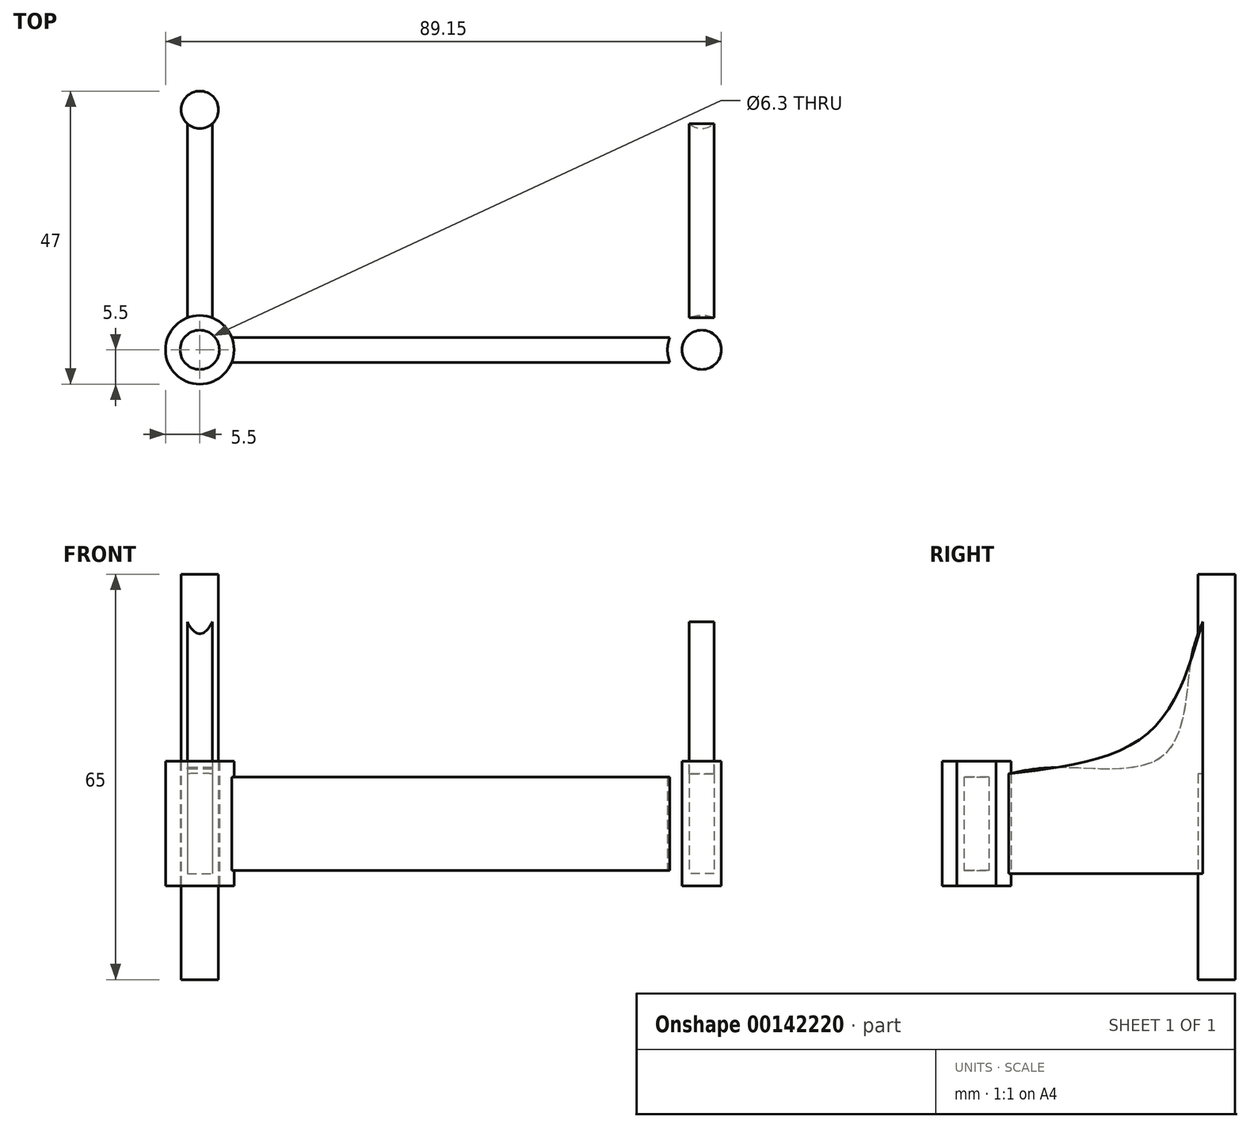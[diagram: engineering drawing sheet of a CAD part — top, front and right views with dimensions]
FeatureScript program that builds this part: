
annotation { "Feature Type Name" : "Feature", "Feature Type Description" : "" }
export const myFeature = defineFeature(function(context is Context, id is Id, definition is map)
    precondition{}
    {
        {
            var Q0;
            Q0=qCreatedBy(makeId("Top.planeOp"),FACE);
            var sketch = newSketch(context, id + "F0", { "sketchPlane" : qUnion([Q0])});
            skLineSegment(sketch, "E0.0", {"start": v(-35.13, -52) * mm, "end": v(0, -52) * mm});
            skLineSegment(sketch, "E1.0", {"start": v(-35.13, -48) * mm, "end": v(0, -48) * mm});
            skCircle(sketch, "E2", {"center": v(-40.25, -11.5) * mm, "radius": 3 * mm});
            skCircle(sketch, "E3", {"center": v(-40.25, -50) * mm, "radius": 3.15 * mm});
            skPoint(sketch, "E4", {"position": v(-42.25, -44.88) * mm});
            skPoint(sketch, "E5", {"position": v(-38.25, -44.88) * mm});
            skPoint(sketch, "E6", {"position": v(-42.25, -13.74) * mm});
            skPoint(sketch, "E7", {"position": v(-38.25, -13.74) * mm});
            skLineSegment(sketch, "E8", {"start": v(-42.25, -44.88) * mm, "end": v(-42.25, -13.74) * mm});
            skLineSegment(sketch, "E9", {"start": v(-38.25, -13.74) * mm, "end": v(-38.25, -44.88) * mm});
            skCircle(sketch, "E10", {"center": v(-40.25, -50) * mm, "radius": 5.5 * mm});
            skPoint(sketch, "E11.MirrorP", {"position": v(38.25, -44.88) * mm});
            skPoint(sketch, "E12.MirrorP", {"position": v(42.25, -44.88) * mm});
            skLineSegment(sketch, "E13.MirrorCS", {"start": v(35.13, -48) * mm, "end": v(0, -48) * mm});
            skLineSegment(sketch, "E14.MirrorCS", {"start": v(42.25, -44.88) * mm, "end": v(42.25, -13.74) * mm});
            skPoint(sketch, "E15.MirrorP", {"position": v(42.25, -13.74) * mm});
            skCircle(sketch, "E16.MirrorC", {"center": v(40.25, -50) * mm, "radius": 5.5 * mm});
            skPoint(sketch, "E17.MirrorP", {"position": v(38.25, -13.74) * mm});
            skCircle(sketch, "E18.MirrorC", {"center": v(40.25, -11.5) * mm, "radius": 3 * mm});
            skLineSegment(sketch, "E19.MirrorCS", {"start": v(38.25, -13.74) * mm, "end": v(38.25, -44.88) * mm});
            skLineSegment(sketch, "E20.MirrorCS", {"start": v(35.13, -52) * mm, "end": v(0, -52) * mm});
            skCircle(sketch, "E21.MirrorC", {"center": v(40.25, -50) * mm, "radius": 3.15 * mm});
            skSolve(sketch);
        }
        {
            var Q0;
            Q0=makeQuery(id+"F0.imprint","IMPRINT",FACE,{"disambiguationData":[TD([[makeQuery(id+"F0.imprint","IMPRINT",EDGE,{"derivedFrom":sQuery(id+"F0.wireOp",EDGE,"E3")}),-1.0]])]});
            var Q1;
            Q1=makeQuery(id+"F0.imprint","IMPRINT",FACE,{"disambiguationData":[TD([[makeQuery(id+"F0.imprint","IMPRINT",EDGE,{"derivedFrom":sQuery(id+"F0.wireOp",EDGE,"E21.MirrorC")}),1.0]])]});
            extrude(context, id + "F1", {"entities" : qUnion([Q0, Q1]), "depth" : 20 * mm, "symmetric" : true});
        }
        {
            var Q0;
            {var subQ2=sQuery(id+"F0.wireOp",EDGE,"E0.0");Q0=makeQuery(id+"F0.imprint","IMPRINT",FACE,{"disambiguationData":[TD([[makeQuery(id+"F0.imprint","IMPRINT",EDGE,{"derivedFrom":subQ2}),1.0]])]});}
            extrude(context, id + "F2", {"entities" : qUnion([Q0]), "operationType" : NewBodyOperationType.ADD, "depth" : 15 * mm, "symmetric" : true});
        }
        {
            var Q0;
            {var subQ0=sQuery(id+"F0.wireOp",EDGE,"E14.MirrorCS");Q0=makeQuery(id+"F0.imprint","IMPRINT",FACE,{"disambiguationData":[TD([[makeQuery(id+"F0.imprint","IMPRINT",EDGE,{"derivedFrom":subQ0}),1.0]])]});}
            var Q1;
            {var subQ0=sQuery(id+"F0.wireOp",EDGE,"E8");Q1=makeQuery(id+"F0.imprint","IMPRINT",FACE,{"disambiguationData":[TD([[makeQuery(id+"F0.imprint","IMPRINT",EDGE,{"derivedFrom":subQ0}),-1.0]])]});}
            extrude(context, id + "F3", {"entities" : qUnion([Q0, Q1]), "operationType" : NewBodyOperationType.ADD, "depth" : 16 * mm, "symmetric" : true});
        }
        {
            var Q0;
            {var subQ0=sQuery(id+"F0.wireOp",EDGE,"E2");var subQ1=makeQuery(id+"F0.imprint","INTERSECT",VERTEX,{"derivedFrom":[subQ0,sQuery(id+"F0.wireOp",EDGE,"E8")]});Q0=makeQuery(id+"F0.imprint","IMPRINT",FACE,{"disambiguationData":[TD([[makeQuery(id+"F0.imprint","IMPRINT",EDGE,{"disambiguationData":[TD([[subQ1,-1.0]])],"derivedFrom":subQ0}),1.0]])]});}
            var Q1;
            {var subQ0=sQuery(id+"F0.wireOp",EDGE,"E18.MirrorC");var subQ1=makeQuery(id+"F0.imprint","INTERSECT",VERTEX,{"derivedFrom":[sQuery(id+"F0.wireOp",EDGE,"E14.MirrorCS"),subQ0]});Q1=makeQuery(id+"F0.imprint","IMPRINT",FACE,{"disambiguationData":[TD([[makeQuery(id+"F0.imprint","IMPRINT",EDGE,{"disambiguationData":[TD([[subQ1,-1.0]])],"derivedFrom":subQ0}),-1.0]])]});}
            extrude(context, id + "F4", {"entities" : qUnion([Q0, Q1]), "operationType" : NewBodyOperationType.ADD, "depth" : 40 * mm, "hasSecondDirection" : true, "secondDirectionOppositeDirection" : true, "secondDirectionDepth" : 25 * mm});
        }
        {
            var Q0;
            Q0=makeQuery(id+"F3.opExtrude","SWEPT_FACE",FACE,{"disambiguationData":[OSD([sQuery(id+"F0.wireOp",EDGE,"E14.MirrorCS")])]});
            var sketch = newSketch(context, id + "F5", { "sketchPlane" : qUnion([Q0])});
            skFitSpline(sketch, "E22", {"points": [v(-44.88, 8) * mm, v(-22.66, 14.38) * mm, v(-13.74, 32.4) * mm], "startDerivative": vector(49.25, 5.87) * mm, "endDerivative": vector(12.6, 43.37) * mm});
            skLineSegment(sketch, "E23", {"start": v(-13.74, 32.4) * mm, "end": v(-13.74, 8) * mm});
            skLineSegment(sketch, "E24", {"start": v(-13.74, 8) * mm, "end": v(-44.88, 8) * mm});
            skSolve(sketch);
        }
        {
            var Q0;
            Q0 = qSketchRegion(id + "F5", true);
            var Q1;
            Q1=makeQuery(id+"F3.opExtrude","SWEPT_FACE",FACE,{"disambiguationData":[OSD([sQuery(id+"F0.wireOp",EDGE,"E9")])]});
            var Q2;
            Q2 = qSketchRegion(id + "F7", true);
            extrude(context, id + "F6", {"entities" : qUnion([Q0, Q1, Q2]), "operationType" : NewBodyOperationType.ADD, "oppositeDirection" : true, "depth" : 4 * mm});
        }
        {
            var Q0;
            Q0=makeQuery(id+"F3.opExtrude","SWEPT_FACE",FACE,{"disambiguationData":[OSD([sQuery(id+"F0.wireOp",EDGE,"E9")])]});
            var sketch = newSketch(context, id + "F7", { "sketchPlane" : qUnion([Q0])});
            skLineSegment(sketch, "E25", {"start": v(-13.74, 8) * mm, "end": v(-44.88, 8) * mm});
            skLineSegment(sketch, "E26.0.0", {"start": v(-44.88, -8) * mm, "end": v(-13.74, -8) * mm});
            skFitSpline(sketch, "E26.0.2", {"points": [v(-13.74, 32.4) * mm, v(-15.76, 25.43) * mm, v(-19.96, 10.97) * mm, v(-36.38, 9.01) * mm, v(-44.88, 8) * mm]});
            skLineSegment(sketch, "E26.0.3", {"start": v(-44.88, 8) * mm, "end": v(-44.88, -8) * mm});
            skLineSegment(sketch, "E27", {"start": v(-13.74, 32.4) * mm, "end": v(-13.74, 8) * mm});
            skSolve(sketch);
        }
        {
            var Q0;
            Q0=makeQuery(id+"F7.imprint","IMPRINT",FACE,{"disambiguationData":[TD([[makeQuery(id+"F7.imprint","IMPRINT",EDGE,{"derivedFrom":sQuery(id+"F7.wireOp",EDGE,"E25")}),-1.0]])]});
            extrude(context, id + "F8", {"entities" : qUnion([Q0]), "operationType" : NewBodyOperationType.ADD, "oppositeDirection" : true, "depth" : 4 * mm});
        }
    });
